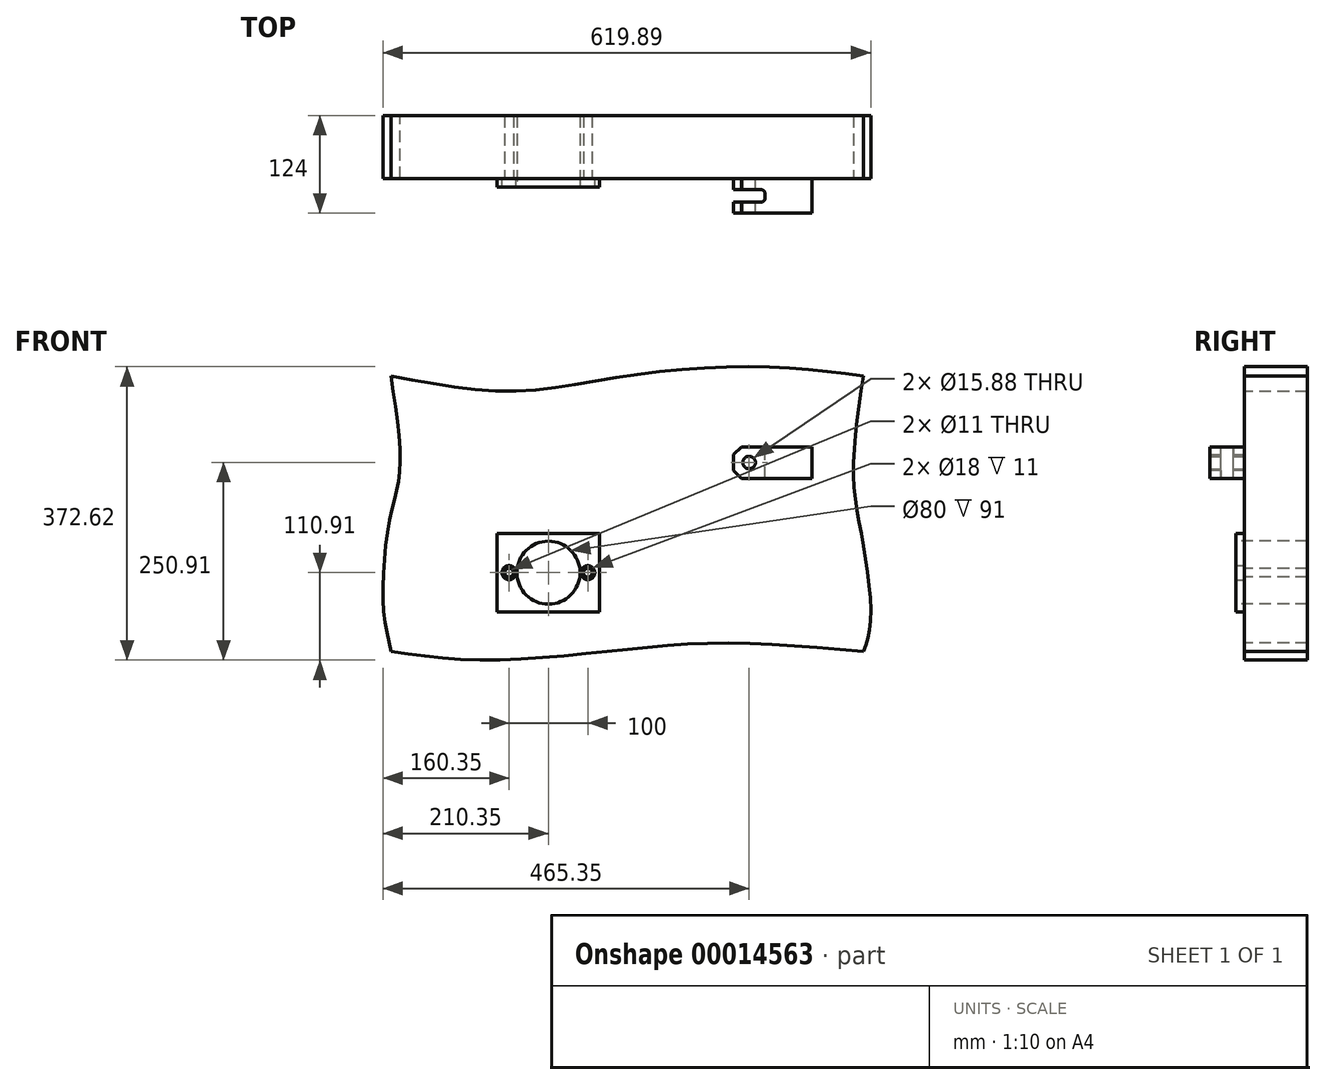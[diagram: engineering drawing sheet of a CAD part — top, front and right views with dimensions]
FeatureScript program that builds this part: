
annotation { "Feature Type Name" : "Feature", "Feature Type Description" : "" }
export const myFeature = defineFeature(function(context is Context, id is Id, definition is map)
    precondition{}
    {
        {
            var Q0;
            Q0=qCreatedBy(makeId("Front.planeOp"),FACE);
            var sketch = newSketch(context, id + "F0", { "sketchPlane" : qUnion([Q0])});
            skPoint(sketch, "E0.rect.middle", {"position": v(0, 0) * mm});
            skFitSpline(sketch, "E1", {"points": [v(-300, 175) * mm, v(-288.67, 56.04) * mm, v(-300, 0) * mm, v(-310.2, -107.97) * mm, v(-300, -175) * mm], "startDerivative": vector(67.45, -453.57) * mm, "endDerivative": vector(63.04, -272.45) * mm});
            skFitSpline(sketch, "E2", {"points": [v(-300, 175) * mm, v(-144.91, 155.47) * mm, v(0, 175) * mm, v(173, 186.5) * mm, v(300, 175) * mm], "startDerivative": vector(619.8, -119.72) * mm, "endDerivative": vector(524.3, -67.94) * mm});
            skFitSpline(sketch, "E3", {"points": [v(300, 175) * mm, v(287.61, 47.81) * mm, v(300, -40.21) * mm, v(309.15, -137.74) * mm, v(300, -175) * mm], "startDerivative": vector(-65.1, -439.57) * mm, "endDerivative": vector(-70.97, -189.85) * mm});
            skFitSpline(sketch, "E4", {"points": [v(300, -175) * mm, v(120.43, -164.33) * mm, v(-25.86, -175) * mm, v(-186.7, -185.87) * mm, v(-300, -175) * mm], "startDerivative": vector(-676.6, 60.09) * mm, "endDerivative": vector(-491.54, 71) * mm});
            skSolve(sketch);
        }
        {
            var Q0;
            Q0 = qSketchRegion(id + "F0", true);
            extrude(context, id + "F1", {"entities" : qUnion([Q0]), "oppositeDirection" : true, "depth" : 80 * mm});
        }
        {
            var Q0;
            Q0=makeQuery(id+"F1.opExtrude","CAP_FACE",FACE,{"disambiguationData":[OSD([sQuery(id+"F0.wireOp",EDGE,"E1"),sQuery(id+"F0.wireOp",EDGE,"E2"),sQuery(id+"F0.wireOp",EDGE,"E3"),sQuery(id+"F0.wireOp",EDGE,"E4")])],"isStart":true});
            var sketch = newSketch(context, id + "F2", { "sketchPlane" : qUnion([Q0])});
            skLineSegment(sketch, "E5", {"start": v(-100, 270) * mm, "end": v(-100, -299.44) * mm, "construction": true});
            skLineSegment(sketch, "E6", {"start": v(-457.85, -75) * mm, "end": v(206.33, -75) * mm, "construction": true});
            skCircle(sketch, "E7", {"center": v(-100, -75) * mm, "radius": 40 * mm});
            skLineSegment(sketch, "E8.0", {"start": v(-150, 270) * mm, "end": v(-150, -299.44) * mm, "construction": true});
            skCircle(sketch, "E9", {"center": v(-150, -75) * mm, "radius": 5.5 * mm});
            skCircle(sketch, "E10.0.MirrorC", {"center": v(-50, -75) * mm, "radius": 5.5 * mm});
            skSolve(sketch);
        }
        {
            var Q0;
            Q0 = qSketchRegion(id + "F2", true);
            extrude(context, id + "F3", {"entities" : qUnion([Q0]), "operationType" : NewBodyOperationType.REMOVE, "endBound" : BoundingType.THROUGH_ALL, "oppositeDirection" : true, "depth" : 25 * mm});
        }
        {
            var Q0;
            Q0=makeQuery(id+"F1.opExtrude","CAP_FACE",FACE,{"disambiguationData":[OSD([sQuery(id+"F0.wireOp",EDGE,"E1"),sQuery(id+"F0.wireOp",EDGE,"E2"),sQuery(id+"F0.wireOp",EDGE,"E3"),sQuery(id+"F0.wireOp",EDGE,"E4")])],"isStart":true});
            var sketch = newSketch(context, id + "F4", { "sketchPlane" : qUnion([Q0])});
            skLineSegment(sketch, "E11", {"start": v(-100, -75) * mm, "end": v(-100, -205.65) * mm, "construction": true});
            skLineSegment(sketch, "E12", {"start": v(-100, -75) * mm, "end": v(-353.74, -75) * mm, "construction": true});
            skLineSegment(sketch, "E13.0", {"start": v(-165, -25) * mm, "end": v(-165, -125) * mm});
            skLineSegment(sketch, "E14.0", {"start": v(-35, -125) * mm, "end": v(-165, -125) * mm});
            skLineSegment(sketch, "E15.0.MirrorCS", {"start": v(-35, -25) * mm, "end": v(-165, -25) * mm});
            skLineSegment(sketch, "E16.0.MirrorCS", {"start": v(-35, -25) * mm, "end": v(-35, -125) * mm});
            skPoint(sketch, "E17.orphan", {"position": v(-165, -75) * mm});
            skPoint(sketch, "E18.orphan", {"position": v(-100, -25) * mm});
            skPoint(sketch, "E19.orphan", {"position": v(-35, -75) * mm});
            skPoint(sketch, "E20.orphan", {"position": v(-100, -125) * mm});
            skPoint(sketch, "E21.orphan", {"position": v(-353.74, -25) * mm});
            skPoint(sketch, "E22.orphan", {"position": v(-353.74, -125) * mm});
            skPoint(sketch, "E23.orphan", {"position": v(-165, -205.65) * mm});
            skPoint(sketch, "E24.orphan", {"position": v(-35, -205.65) * mm});
            skCircle(sketch, "E25.0", {"center": v(-100, -75) * mm, "radius": 40 * mm});
            skCircle(sketch, "E26", {"center": v(-150, -75) * mm, "radius": 9 * mm});
            skCircle(sketch, "E27.0.MirrorC", {"center": v(-50, -75) * mm, "radius": 9 * mm});
            skSolve(sketch);
        }
        {
            var Q0;
            Q0 = qSketchRegion(id + "F4", true);
            extrude(context, id + "F5", {"entities" : qUnion([Q0]), "operationType" : NewBodyOperationType.ADD, "depth" : 11 * mm});
        }
        {
            var Q0;
            {var subQ0=sQuery(id+"F0.wireOp",EDGE,"E1");var subQ1=sQuery(id+"F0.wireOp",EDGE,"E2");var subQ2=sQuery(id+"F0.wireOp",EDGE,"E3");var subQ3=sQuery(id+"F0.wireOp",EDGE,"E4");Q0=makeQuery(id+"F5.boolean.opBoolean","SPLIT",FACE,{"disambiguationData":[TD([makeQuery(id+"F1.opExtrude","SWEPT_FACE",FACE,{"disambiguationData":[OSD([subQ0])]})])],"derivedFrom":makeQuery(id+"F1.opExtrude","CAP_FACE",FACE,{"disambiguationData":[OSD([subQ0,subQ1,subQ2,subQ3])],"isStart":true})});}
            var sketch = newSketch(context, id + "F6", { "sketchPlane" : qUnion([Q0])});
            skCircle(sketch, "E28.0", {"center": v(-100, -75) * mm, "radius": 40 * mm, "construction": true});
            skLineSegment(sketch, "E29", {"start": v(-100, -75) * mm, "end": v(-100, 236.24) * mm, "construction": true});
            skLineSegment(sketch, "E30", {"start": v(-100, -75) * mm, "end": v(374.63, -75) * mm, "construction": true});
            skLineSegment(sketch, "E31.0", {"start": v(135, -75) * mm, "end": v(135, 236.24) * mm, "construction": true});
            skLineSegment(sketch, "E32.0", {"start": v(-100, 45) * mm, "end": v(374.63, 45) * mm, "construction": true});
            skLineSegment(sketch, "E33.0", {"start": v(235, -75) * mm, "end": v(235, 236.24) * mm, "construction": true});
            skLineSegment(sketch, "E34.0", {"start": v(-100, 85) * mm, "end": v(374.63, 85) * mm, "construction": true});
            skLineSegment(sketch, "E35.0", {"start": v(155, 45) * mm, "end": v(155, 85) * mm, "construction": true});
            skLineSegment(sketch, "E36.bottom", {"start": v(135, 85) * mm, "end": v(235, 85) * mm});
            skLineSegment(sketch, "E36.top", {"start": v(135, 45) * mm, "end": v(235, 45) * mm});
            skLineSegment(sketch, "E36.left", {"start": v(135, 85) * mm, "end": v(135, 45) * mm});
            skLineSegment(sketch, "E36.right", {"start": v(235, 85) * mm, "end": v(235, 45) * mm});
            skCircle(sketch, "E37", {"center": v(155, 65) * mm, "radius": 7.94 * mm});
            skSolve(sketch);
        }
        {
            var Q0;
            Q0 = qSketchRegion(id + "F6", true);
            extrude(context, id + "F7", {"entities" : qUnion([Q0]), "depth" : 44 * mm});
        }
        {
            var Q0;
            Q0=makeQuery(id+"F7.opExtrude","SWEPT_FACE",FACE,{"disambiguationData":[OSD([sQuery(id+"F6.wireOp",EDGE,"E36.bottom")])]});
            var sketch = newSketch(context, id + "F8", { "sketchPlane" : qUnion([Q0])});
            skLineSegment(sketch, "E38", {"start": v(135, -22) * mm, "end": v(235, -22) * mm, "construction": true});
            skLineSegment(sketch, "E39.0", {"start": v(175, -44) * mm, "end": v(175, 0) * mm, "construction": true});
            skLineSegment(sketch, "E40.0", {"start": v(135, -14) * mm, "end": v(235, -14) * mm, "construction": true});
            skLineSegment(sketch, "E41.bottom", {"start": v(135, -14) * mm, "end": v(175, -14) * mm});
            skLineSegment(sketch, "E41.top", {"start": v(135, -30) * mm, "end": v(175, -30) * mm});
            skLineSegment(sketch, "E41.left", {"start": v(135, -14) * mm, "end": v(135, -30) * mm});
            skLineSegment(sketch, "E41.right", {"start": v(175, -14) * mm, "end": v(175, -30) * mm});
            skSolve(sketch);
        }
        {
            var Q0;
            Q0 = qSketchRegion(id + "F8", true);
            extrude(context, id + "F9", {"entities" : qUnion([Q0]), "operationType" : NewBodyOperationType.REMOVE, "endBound" : BoundingType.THROUGH_ALL, "oppositeDirection" : true, "depth" : 25 * mm});
        }
        {
            var Q0;
            {var subQ0=sQuery(id+"F6.wireOp",EDGE,"E36.bottom");var subQ1=sQuery(id+"F6.wireOp",EDGE,"E36.left");Q0=makeQuery(id+"F9.boolean.opBoolean","SPLIT",EDGE,{"disambiguationData":[TD([makeQuery(id+"F9.opExtrude","SWEPT_FACE",FACE,{"disambiguationData":[OSD([sQuery(id+"F8.wireOp",EDGE,"E41.bottom")])]})])],"derivedFrom":makeQuery(id+"F7.opExtrude","SWEPT_EDGE",EDGE,{"disambiguationData":[OSD([subQ0,subQ1])]})});}
            var Q1;
            {var subQ0=sQuery(id+"F6.wireOp",EDGE,"E36.bottom");var subQ1=sQuery(id+"F6.wireOp",EDGE,"E36.left");Q1=makeQuery(id+"F9.boolean.opBoolean","SPLIT",EDGE,{"disambiguationData":[TD([makeQuery(id+"F9.opExtrude","SWEPT_FACE",FACE,{"disambiguationData":[OSD([sQuery(id+"F8.wireOp",EDGE,"E41.top")])]})])],"derivedFrom":makeQuery(id+"F7.opExtrude","SWEPT_EDGE",EDGE,{"disambiguationData":[OSD([subQ0,subQ1])]})});}
            var Q2;
            {var subQ0=sQuery(id+"F6.wireOp",EDGE,"E36.top");var subQ1=sQuery(id+"F6.wireOp",EDGE,"E36.left");Q2=makeQuery(id+"F9.boolean.opBoolean","SPLIT",EDGE,{"disambiguationData":[TD([makeQuery(id+"F9.opExtrude","SWEPT_FACE",FACE,{"disambiguationData":[OSD([sQuery(id+"F8.wireOp",EDGE,"E41.bottom")])]})])],"derivedFrom":makeQuery(id+"F7.opExtrude","SWEPT_EDGE",EDGE,{"disambiguationData":[OSD([subQ0,subQ1])]})});}
            var Q3;
            {var subQ0=sQuery(id+"F6.wireOp",EDGE,"E36.top");var subQ1=sQuery(id+"F6.wireOp",EDGE,"E36.left");Q3=makeQuery(id+"F9.boolean.opBoolean","SPLIT",EDGE,{"disambiguationData":[TD([makeQuery(id+"F9.opExtrude","SWEPT_FACE",FACE,{"disambiguationData":[OSD([sQuery(id+"F8.wireOp",EDGE,"E41.top")])]})])],"derivedFrom":makeQuery(id+"F7.opExtrude","SWEPT_EDGE",EDGE,{"disambiguationData":[OSD([subQ0,subQ1])]})});}
            chamfer(context, id + "F10", {"entities" : qUnion([Q0, Q1, Q2, Q3]), "width" : 10 * mm, "tangentPropagation" : true});
        }
        {
            var Q0;
            Q0=makeQuery(id+"F9.boolean.opBoolean","COPY",EDGE,{"derivedFrom":makeQuery(id+"F9.opExtrude","SWEPT_EDGE",EDGE,{"disambiguationData":[OSD([sQuery(id+"F8.wireOp",EDGE,"E41.bottom"),sQuery(id+"F8.wireOp",EDGE,"E41.right")])]})});
            var Q1;
            Q1=makeQuery(id+"F9.boolean.opBoolean","COPY",EDGE,{"derivedFrom":makeQuery(id+"F9.opExtrude","SWEPT_EDGE",EDGE,{"disambiguationData":[OSD([sQuery(id+"F8.wireOp",EDGE,"E41.top"),sQuery(id+"F8.wireOp",EDGE,"E41.right")])]})});
            fillet(context, id + "F11", {"entities" : qUnion([Q0, Q1]), "radius" : 5 * mm, "tangentPropagation" : true, "allowEdgeOverflow" : false});
        }
    });
